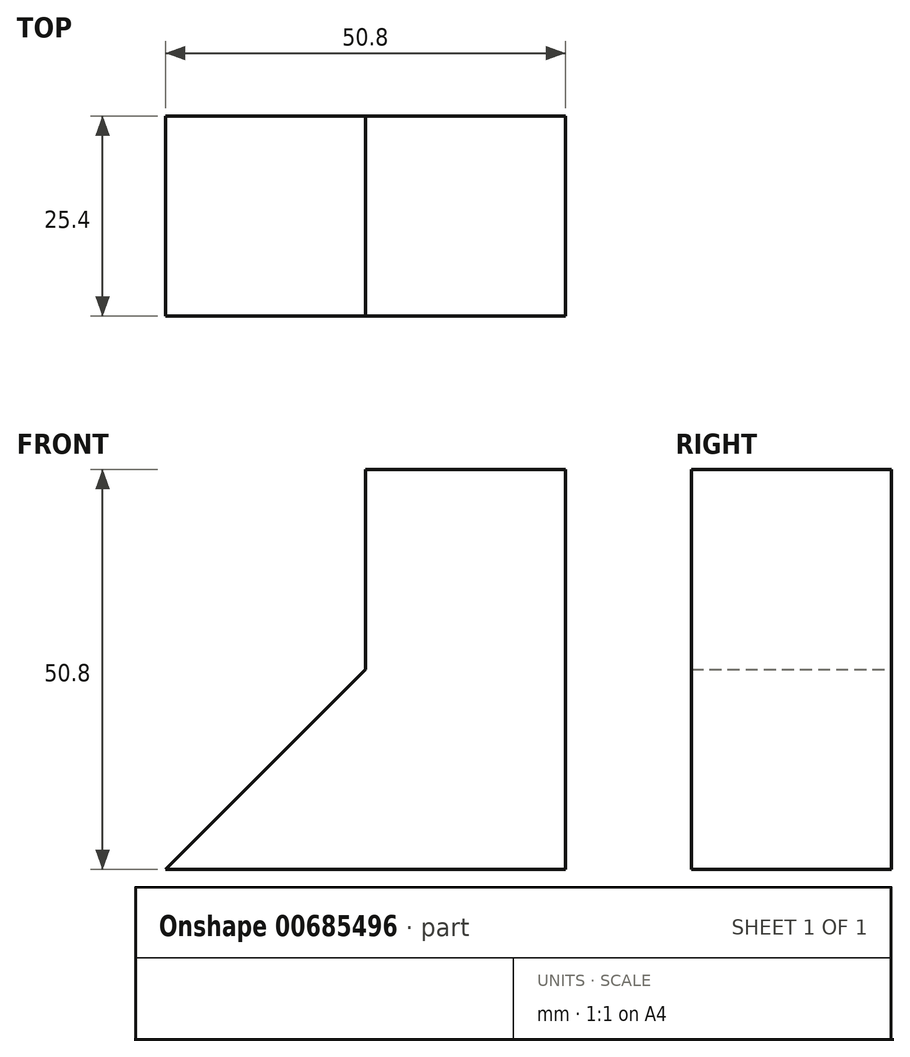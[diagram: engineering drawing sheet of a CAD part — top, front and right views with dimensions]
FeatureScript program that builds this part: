
annotation { "Feature Type Name" : "Feature", "Feature Type Description" : "" }
export const myFeature = defineFeature(function(context is Context, id is Id, definition is map)
    precondition{}
    {
        {
            var Q0;
            Q0=qCreatedBy(makeId("Front.planeOp"),FACE);
            var sketch = newSketch(context, id + "F0", { "sketchPlane" : qUnion([Q0])});
            skLineSegment(sketch, "E0", {"start": v(-31.6, 32.56) * mm, "end": v(-31.6, 57.96) * mm});
            skLineSegment(sketch, "E1", {"start": v(-31.6, 57.96) * mm, "end": v(-6.2, 57.96) * mm});
            skLineSegment(sketch, "E2", {"start": v(-6.2, 57.96) * mm, "end": v(-6.2, 7.16) * mm});
            skLineSegment(sketch, "E3", {"start": v(-6.2, 7.16) * mm, "end": v(-57, 7.16) * mm});
            skLineSegment(sketch, "E4", {"start": v(-57, 7.16) * mm, "end": v(-31.6, 32.56) * mm});
            skSolve(sketch);
        }
        {
            var Q0;
            Q0 = qSketchRegion(id + "F0", true);
            extrude(context, id + "F1", {"entities" : qUnion([Q0]), "depth" : 25.4 * mm, "offsetDistance" : 25.4 * mm});
        }
    });
